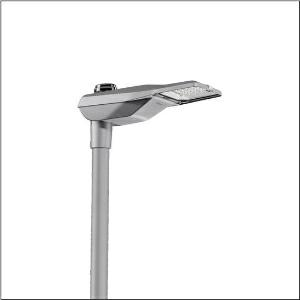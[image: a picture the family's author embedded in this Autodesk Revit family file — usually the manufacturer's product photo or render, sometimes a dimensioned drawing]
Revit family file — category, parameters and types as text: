
# Revit family: streetlight_sl_21_micro___st1_0a_5xe5d37n08cb_defe
name_source: partatom
category: Lighting Fixtures
units: mm (PartAtom-declared; Revit-internal decimal feet)

## family parameters
Cut with Voids When Loaded = No
Host = Face
Light Source = No
Part Type = Normal
Room Calculation Point = No
Round Connector Dimension = Use Diameter
Shared = No

## types (1)
- --- (1 x LED, 2290 lm, 15.8 W, 3000K)
    Apparent Load = 16 VA
    CIE Flux Codes = 37 72 97 100 100
    Color Rendering = 70
    Color Temperature = 3000K
    Default Elevation = 1800 mm
    Description = Streetlight SL 21 micro, mast luminaire, primary light control with lens, of PMMA, primary optical cover: cover, of toughened safety glass, transparent, light distribution: ST1.0a, light emission: direct distribution, primary light characteristic: asymmetric, installation type: post-top, LED, 3G 1.5mm², High Power LED, rated luminous flux: 2.290lm, luminous efficacy: 145lm/W, light colour: 730, colour temperature: 3000K, control: overheat protection, presetting dimming linear, constant luminous flux control, time-dependent luminous flux control, flexible luminous flux parameterisation, mains connection: 230..240V, AC, 50/60Hz, connection cable pre-assembled, cable length: 6,5m, wiring characteristics: H07RN-F, start of lifetime: 16W, end of service life: 16W, reduction: 8W, luminaire housing, of diecast aluminium (EN AC-44300), powder-coated, Siteco® metallic grey (DB 702S), corrosivity category C5 mid according to DIN EN ISO 12944, multi-level sealing system, sealing non-destructively replaceable, inclination adjustable: 0°, 5°, 10°, 15°, length: 528mm, width: 235mm, height: 110mm, spigot size: 76/60mm (post-top), protection rating (complete): IP66, insulation class (complete): insulation class I (protective earthing), certification: CE, ENEC, ENEC+, VDE, impact resistance: IK09, permissible operating ambient temperature for outdoor applications: -40..+50°C, standard-compliant lighting for roads and squares, packaging unit: 1 piece

Light Distribution: ST1.0a
    Height = 110 mm
    Lamp = 1 x LED
    Lamp Light Flux = 2290 lm
    Lamp Power = 15.8 W
    Lamp count = 1
    Length = 528 mm
    Luminous efficacy = 145 lm/W
    Manufacturer = Siteco
    ModVariant = No
    Model = 5XE5D37N08CB
    Number of Poles = 1
    OnlyDefault = Yes
    Power Factor = 1
    Product Name = Streetlight SL 21 micro | ST1.0a
    Product group = mast luminaire | pylon top
    ProductGroupID = 6100
    Protection Class = Protection class I
    Protection Degree = IP 66
    RLX_Detail_Level = 1
    RLX_Emergency_Light_Flux = 0 lm
    RLX_Emergency_Type = 0
    RLX_Emergency_Type_DB = No
    RlxData = <blob elided: 98133 chars, md5=13a5303d>
    Socket = socket
    Standby Power = 0 W
    System Light Flux = 2290 lm
    System Power = 16 W
    Type Comments = factory setting: luminous flux: 100 % | dim-lin: 254 | 300 mA
    Type Image = l_1294375.jpg
    URL = http://relux.com
    VarID = @adj_085961
    Voltage = 0 V
    Weight = 0.00 kg
    Width = 235 mm

## geometry (parser evidence)
native form markers: Blend x4, Sweep x10
no freeform markers — native parametric forms only
